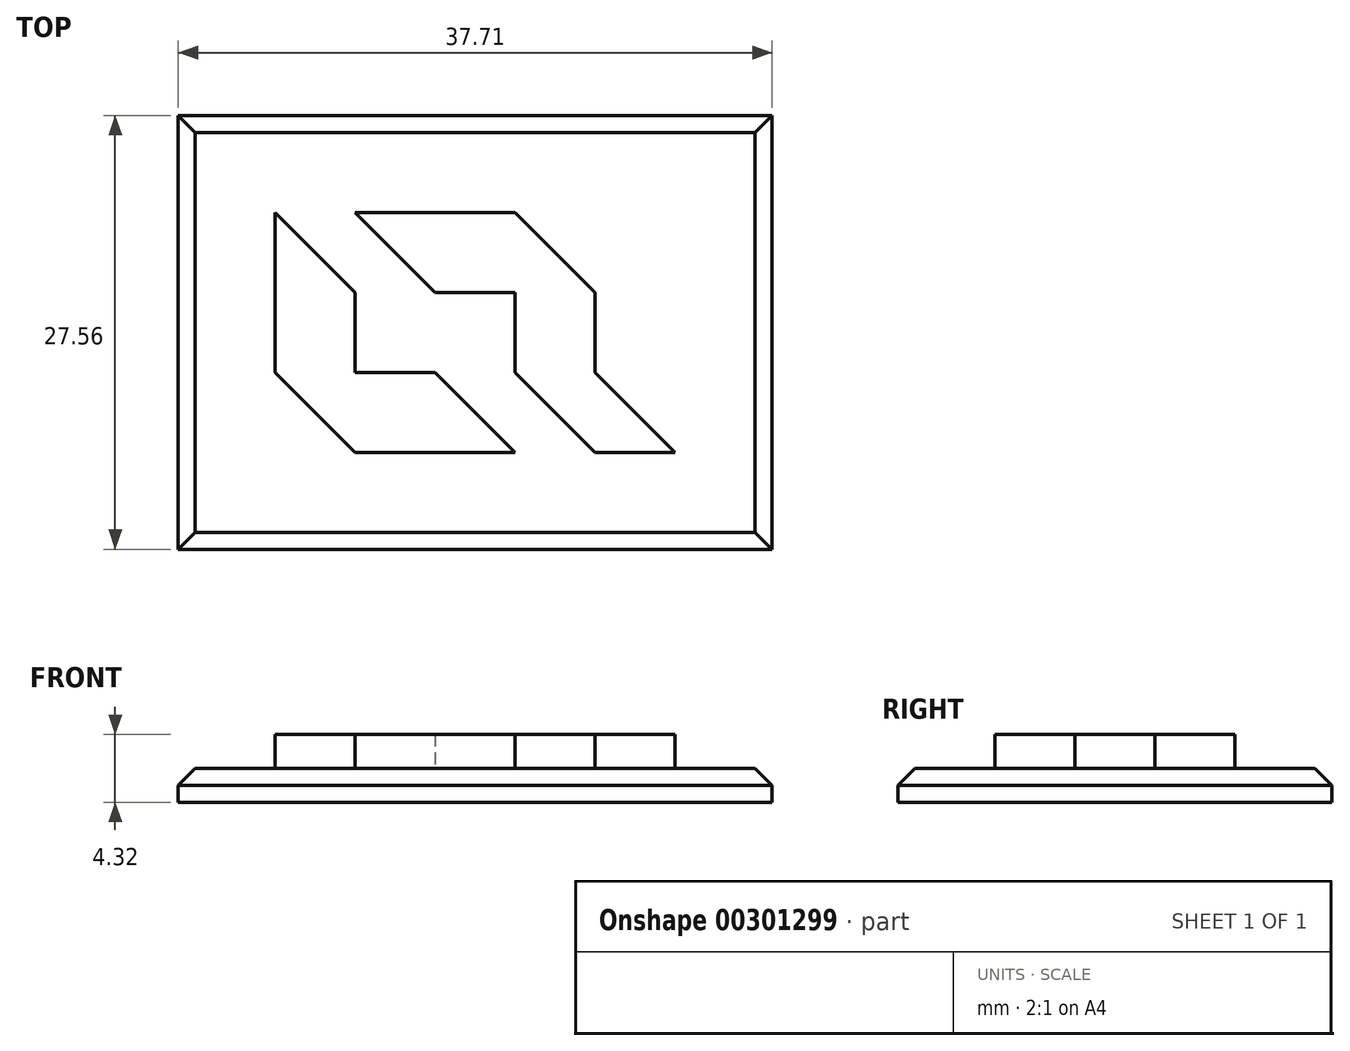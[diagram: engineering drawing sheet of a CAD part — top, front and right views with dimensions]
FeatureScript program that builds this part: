
annotation { "Feature Type Name" : "Feature", "Feature Type Description" : "" }
export const myFeature = defineFeature(function(context is Context, id is Id, definition is map)
    precondition{}
    {
        {
            var Q0;
            Q0=qCreatedBy(makeId("Top.planeOp"),FACE);
            var sketch = newSketch(context, id + "F0", { "sketchPlane" : qUnion([Q0])});
            skLineSegment(sketch, "E0", {"start": v(-17, 16.64) * mm, "end": v(-17, 11.56) * mm});
            skLineSegment(sketch, "E1", {"start": v(-17, 11.56) * mm, "end": v(-11.92, 11.56) * mm});
            skLineSegment(sketch, "E2", {"start": v(-11.92, 11.56) * mm, "end": v(-17, 16.64) * mm});
            skLineSegment(sketch, "E3", {"start": v(-11.92, 11.56) * mm, "end": v(-11.92, 1.4) * mm});
            skLineSegment(sketch, "E4", {"start": v(-11.92, 1.4) * mm, "end": v(-17, 6.48) * mm});
            skLineSegment(sketch, "E5", {"start": v(-17, 6.48) * mm, "end": v(-17, 11.56) * mm});
            skLineSegment(sketch, "E6", {"start": v(-11.92, 11.56) * mm, "end": v(-17, 6.48) * mm});
            skLineSegment(sketch, "E7", {"start": v(-17, 6.48) * mm, "end": v(-11.92, 6.48) * mm});
            skLineSegment(sketch, "E8", {"start": v(-11.92, 6.48) * mm, "end": v(-6.84, 6.48) * mm});
            skLineSegment(sketch, "E9", {"start": v(-6.84, 6.48) * mm, "end": v(-1.76, 1.4) * mm});
            skLineSegment(sketch, "E10", {"start": v(-1.76, 1.4) * mm, "end": v(-11.92, 1.4) * mm});
            skLineSegment(sketch, "E11", {"start": v(-1.76, 1.4) * mm, "end": v(3.32, 1.4) * mm, "construction": true});
            skLineSegment(sketch, "E12", {"start": v(-11.92, 16.64) * mm, "end": v(-1.76, 16.64) * mm});
            skLineSegment(sketch, "E13", {"start": v(-1.76, 16.64) * mm, "end": v(3.32, 11.56) * mm});
            skLineSegment(sketch, "E14", {"start": v(3.32, 11.56) * mm, "end": v(-1.76, 11.56) * mm});
            skLineSegment(sketch, "E15", {"start": v(3.32, 11.56) * mm, "end": v(3.32, 6.48) * mm});
            skLineSegment(sketch, "E16", {"start": v(3.32, 6.48) * mm, "end": v(8.4, 1.4) * mm});
            skLineSegment(sketch, "E17", {"start": v(8.4, 1.4) * mm, "end": v(3.32, 1.4) * mm});
            skLineSegment(sketch, "E18", {"start": v(3.32, 1.4) * mm, "end": v(-1.76, 6.48) * mm});
            skLineSegment(sketch, "E19", {"start": v(-1.76, 6.48) * mm, "end": v(-1.76, 11.56) * mm});
            skLineSegment(sketch, "E20", {"start": v(-1.76, 11.56) * mm, "end": v(-6.84, 11.56) * mm});
            skLineSegment(sketch, "E21", {"start": v(-6.84, 11.56) * mm, "end": v(-11.92, 16.64) * mm});
            skLineSegment(sketch, "E22", {"start": v(-6.84, 11.56) * mm, "end": v(-6.84, 16.64) * mm});
            skLineSegment(sketch, "E23", {"start": v(-6.84, 16.64) * mm, "end": v(-1.76, 11.56) * mm});
            skLineSegment(sketch, "E24", {"start": v(-1.76, 16.64) * mm, "end": v(-1.76, 11.56) * mm});
            skLineSegment(sketch, "E25.bottom", {"start": v(-23.15, -4.76) * mm, "end": v(14.56, -4.76) * mm});
            skLineSegment(sketch, "E25.top", {"start": v(-23.15, 22.8) * mm, "end": v(14.56, 22.8) * mm});
            skLineSegment(sketch, "E25.left", {"start": v(-23.15, -4.76) * mm, "end": v(-23.15, 22.8) * mm});
            skLineSegment(sketch, "E25.right", {"start": v(14.56, -4.76) * mm, "end": v(14.56, 22.8) * mm});
            skSolve(sketch);
        }
        {
            var Q0;
            Q0=makeQuery(id+"F0.imprint","IMPRINT",FACE,{"disambiguationData":[TD([[makeQuery(id+"F0.imprint","IMPRINT",EDGE,{"derivedFrom":sQuery(id+"F0.wireOp",EDGE,"E0")}),1.0]])]});
            var Q1;
            Q1=makeQuery(id+"F0.imprint","IMPRINT",FACE,{"disambiguationData":[TD([[makeQuery(id+"F0.imprint","IMPRINT",EDGE,{"derivedFrom":sQuery(id+"F0.wireOp",EDGE,"E1")}),-1.0]])]});
            var Q2;
            {var subQ0=sQuery(id+"F0.wireOp",EDGE,"E6");Q2=makeQuery(id+"F0.imprint","IMPRINT",FACE,{"disambiguationData":[TD([[makeQuery(id+"F0.imprint","IMPRINT",EDGE,{"derivedFrom":subQ0}),1.0]])]});}
            var Q3;
            {var subQ0=sQuery(id+"F0.wireOp",EDGE,"E4");Q3=makeQuery(id+"F0.imprint","IMPRINT",FACE,{"disambiguationData":[TD([[makeQuery(id+"F0.imprint","IMPRINT",EDGE,{"derivedFrom":subQ0}),-1.0]])]});}
            var Q4;
            {var subQ0=sQuery(id+"F0.wireOp",EDGE,"E21");Q4=makeQuery(id+"F0.imprint","IMPRINT",FACE,{"disambiguationData":[TD([[makeQuery(id+"F0.imprint","IMPRINT",EDGE,{"derivedFrom":subQ0}),-1.0]])]});}
            var Q5;
            Q5=makeQuery(id+"F0.imprint","IMPRINT",FACE,{"disambiguationData":[TD([[makeQuery(id+"F0.imprint","IMPRINT",EDGE,{"derivedFrom":sQuery(id+"F0.wireOp",EDGE,"E20")}),-1.0]])]});
            var Q6;
            {var subQ2=sQuery(id+"F0.wireOp",EDGE,"E23");Q6=makeQuery(id+"F0.imprint","IMPRINT",FACE,{"disambiguationData":[TD([[makeQuery(id+"F0.imprint","IMPRINT",EDGE,{"derivedFrom":subQ2}),1.0]])]});}
            var Q7;
            Q7=makeQuery(id+"F0.imprint","IMPRINT",FACE,{"disambiguationData":[TD([[makeQuery(id+"F0.imprint","IMPRINT",EDGE,{"derivedFrom":sQuery(id+"F0.wireOp",EDGE,"E13")}),-1.0]])]});
            var Q8;
            Q8=makeQuery(id+"F0.imprint","IMPRINT",FACE,{"disambiguationData":[TD([[makeQuery(id+"F0.imprint","IMPRINT",EDGE,{"derivedFrom":sQuery(id+"F0.wireOp",EDGE,"E14")}),1.0]])]});
            var Q9;
            {var subQ2=sQuery(id+"F0.wireOp",EDGE,"E8");Q9=makeQuery(id+"F0.imprint","IMPRINT",FACE,{"disambiguationData":[TD([[makeQuery(id+"F0.imprint","IMPRINT",EDGE,{"derivedFrom":subQ2}),-1.0]])]});}
            extrude(context, id + "F1", {"entities" : qUnion([Q0, Q1, Q2, Q3, Q4, Q5, Q6, Q7, Q8, Q9]), "depth" : 4.32 * mm});
        }
        {
            var Q0;
            Q0=makeQuery(id+"F0.imprint","IMPRINT",FACE,{"disambiguationData":[TD([[makeQuery(id+"F0.imprint","IMPRINT",EDGE,{"derivedFrom":sQuery(id+"F0.wireOp",EDGE,"E0")}),-1.0]])]});
            extrude(context, id + "F2", {"entities" : qUnion([Q0]), "operationType" : NewBodyOperationType.ADD, "depth" : 2.16 * mm});
        }
        {
            var Q0;
            Q0=makeQuery(id+"F2.opExtrude","CAP_EDGE",EDGE,{"disambiguationData":[OSD([sQuery(id+"F0.wireOp",EDGE,"E25.top")])],"isStart":false});
            var Q1;
            Q1=makeQuery(id+"F2.opExtrude","CAP_EDGE",EDGE,{"disambiguationData":[OSD([sQuery(id+"F0.wireOp",EDGE,"E25.left")])],"isStart":false});
            var Q2;
            Q2=makeQuery(id+"F2.opExtrude","CAP_EDGE",EDGE,{"disambiguationData":[OSD([sQuery(id+"F0.wireOp",EDGE,"E25.right")])],"isStart":false});
            var Q3;
            Q3=makeQuery(id+"F2.opExtrude","CAP_EDGE",EDGE,{"disambiguationData":[OSD([sQuery(id+"F0.wireOp",EDGE,"E25.bottom")])],"isStart":false});
            chamfer(context, id + "F3", {"entities" : qUnion([Q0, Q1, Q2, Q3]), "width" : 1.08 * mm, "tangentPropagation" : true});
        }
    });
